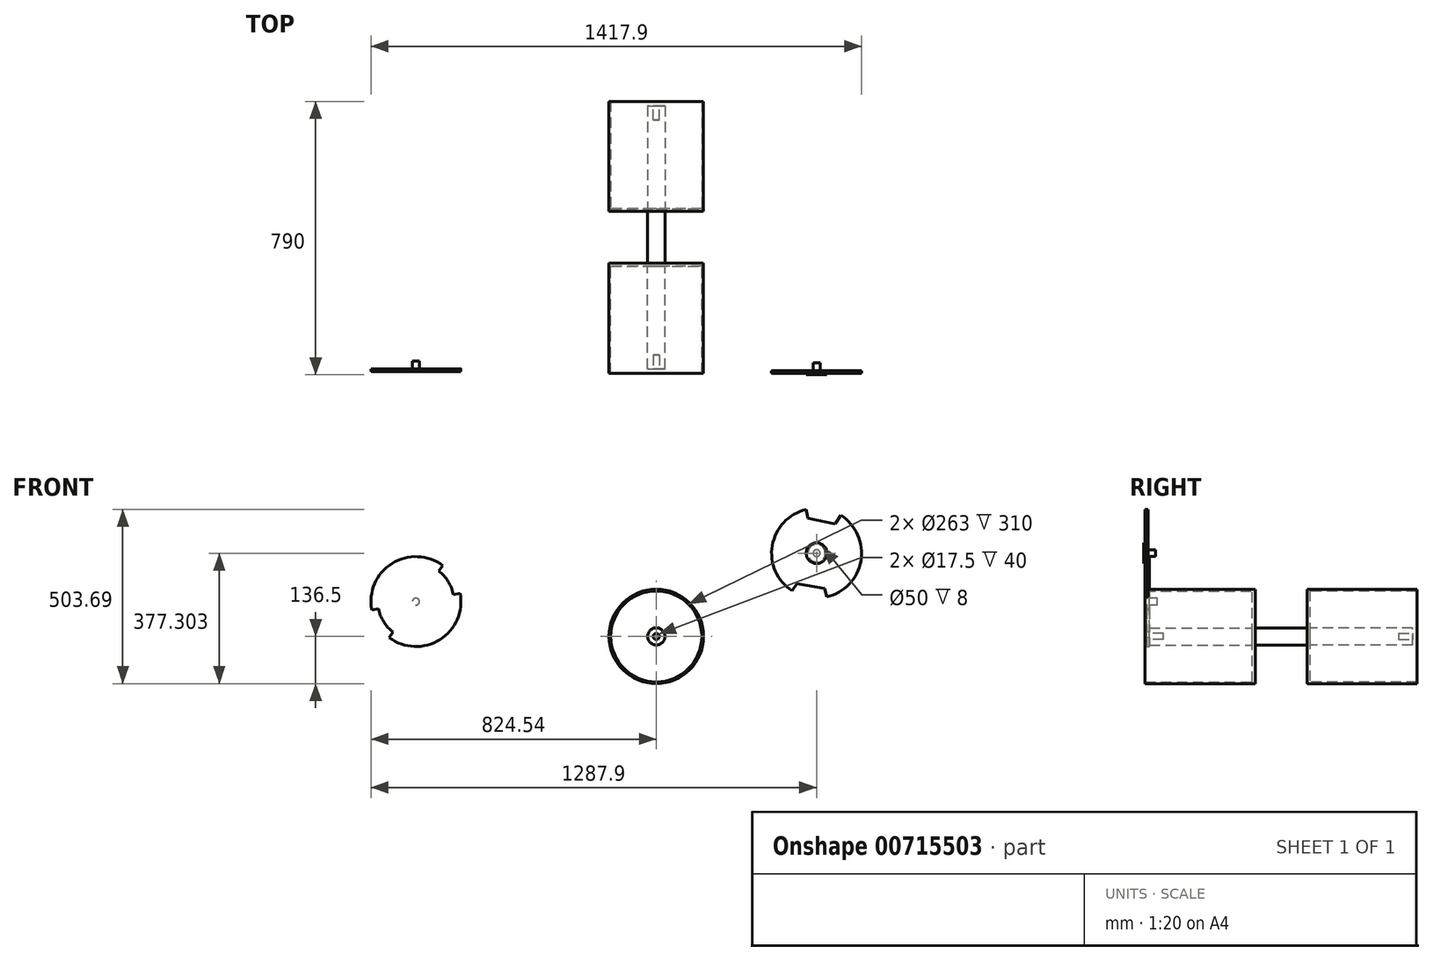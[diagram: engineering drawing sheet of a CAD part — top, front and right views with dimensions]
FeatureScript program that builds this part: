
annotation { "Feature Type Name" : "Feature", "Feature Type Description" : "" }
export const myFeature = defineFeature(function(context is Context, id is Id, definition is map)
    precondition{}
    {
        {
            var Q0;
            Q0=qCreatedBy(makeId("Front.planeOp"),FACE);
            var sketch = newSketch(context, id + "F0", { "sketchPlane" : qUnion([Q0])});
            skCircle(sketch, "E0", {"center": v(0, 0) * mm, "radius": 25 * mm});
            skSolve(sketch);
        }
        {
            var Q0;
            Q0 = qSketchRegion(id + "F0", true);
            extrude(context, id + "F1", {"entities" : qUnion([Q0]), "depth" : 75 * mm, "offsetDistance" : 25 * mm});
        }
        {
            var Q0;
            Q0=makeQuery(id+"F1.opExtrude","CAP_FACE",FACE,{"disambiguationData":[OSD([sQuery(id+"F0.wireOp",EDGE,"E0")])],"isStart":false});
            var sketch = newSketch(context, id + "F2", { "sketchPlane" : qUnion([Q0])});
            skCircle(sketch, "E1", {"center": v(0, 0) * mm, "radius": 136.5 * mm});
            skSolve(sketch);
        }
        {
            var Q0;
            Q0 = qSketchRegion(id + "F2", true);
            extrude(context, id + "F3", {"entities" : qUnion([Q0]), "operationType" : NewBodyOperationType.ADD, "depth" : 8 * mm, "offsetDistance" : 25 * mm});
        }
        {
            var Q0;
            Q0=makeQuery(id+"F3.opExtrude","CAP_FACE",FACE,{"disambiguationData":[OSD([sQuery(id+"F2.wireOp",EDGE,"E1")])],"isStart":false});
            var sketch = newSketch(context, id + "F4", { "sketchPlane" : qUnion([Q0])});
            skCircle(sketch, "E2", {"center": v(0, 0) * mm, "radius": 136.5 * mm});
            skCircle(sketch, "E3", {"center": v(0, 0) * mm, "radius": 131.5 * mm});
            skSolve(sketch);
        }
        {
            var Q0;
            Q0 = qSketchRegion(id + "F4", true);
            extrude(context, id + "F5", {"entities" : qUnion([Q0]), "operationType" : NewBodyOperationType.ADD, "depth" : 310 * mm, "offsetDistance" : 25 * mm});
        }
        {
            var Q0;
            Q0 = qSketchRegion(id + "F0", true);
            extrude(context, id + "F6", {"entities" : qUnion([Q0]), "operationType" : NewBodyOperationType.ADD, "depth" : 380 * mm, "offsetDistance" : 25 * mm});
        }
        {
            var Q0;
            Q0 = qSketchRegion(id + "F0", true);
            extrude(context, id + "F7", {"entities" : qUnion([Q0]), "operationType" : NewBodyOperationType.ADD, "oppositeDirection" : true, "depth" : 75 * mm, "offsetDistance" : 25 * mm});
        }
        {
            var Q0;
            Q0=makeQuery(id+"F7.opExtrude","CAP_FACE",FACE,{"disambiguationData":[OSD([sQuery(id+"F0.wireOp",EDGE,"E0")])],"isStart":false});
            var sketch = newSketch(context, id + "F8", { "sketchPlane" : qUnion([Q0])});
            skCircle(sketch, "E4", {"center": v(0, 0) * mm, "radius": 136.5 * mm});
            skSolve(sketch);
        }
        {
            var Q0;
            Q0 = qSketchRegion(id + "F8", true);
            extrude(context, id + "F9", {"entities" : qUnion([Q0]), "operationType" : NewBodyOperationType.ADD, "depth" : 8 * mm, "offsetDistance" : 25 * mm});
        }
        {
            var Q0;
            Q0=makeQuery(id+"F9.opExtrude","CAP_FACE",FACE,{"disambiguationData":[OSD([sQuery(id+"F8.wireOp",EDGE,"E4")])],"isStart":false});
            var sketch = newSketch(context, id + "F10", { "sketchPlane" : qUnion([Q0])});
            skCircle(sketch, "E5", {"center": v(0, 0) * mm, "radius": 136.5 * mm});
            skCircle(sketch, "E6", {"center": v(0, 0) * mm, "radius": 131.5 * mm});
            skSolve(sketch);
        }
        {
            var Q0;
            Q0 = qSketchRegion(id + "F10", true);
            extrude(context, id + "F11", {"entities" : qUnion([Q0]), "operationType" : NewBodyOperationType.ADD, "depth" : 310 * mm, "offsetDistance" : 25 * mm});
        }
        {
            var Q0;
            Q0 = qSketchRegion(id + "F0", true);
            extrude(context, id + "F12", {"entities" : qUnion([Q0]), "operationType" : NewBodyOperationType.ADD, "oppositeDirection" : true, "depth" : 380 * mm, "offsetDistance" : 25 * mm});
        }
        {
            var Q0;
            Q0=makeQuery(id+"F12.opExtrude","CAP_FACE",FACE,{"disambiguationData":[OSD([sQuery(id+"F0.wireOp",EDGE,"E0")])],"isStart":false});
            var sketch = newSketch(context, id + "F13", { "sketchPlane" : qUnion([Q0])});
            skCircle(sketch, "E7", {"center": v(0, 0) * mm, "radius": 8.75 * mm});
            skSolve(sketch);
        }
        {
            var Q0;
            Q0 = qSketchRegion(id + "F13", true);
            extrude(context, id + "F14", {"entities" : qUnion([Q0]), "operationType" : NewBodyOperationType.REMOVE, "oppositeDirection" : true, "depth" : 40 * mm, "offsetDistance" : 25 * mm});
        }
        {
            var Q0;
            Q0=makeQuery(id+"F6.opExtrude","CAP_FACE",FACE,{"disambiguationData":[OSD([sQuery(id+"F0.wireOp",EDGE,"E0")])],"isStart":false});
            var sketch = newSketch(context, id + "F15", { "sketchPlane" : qUnion([Q0])});
            skCircle(sketch, "E8", {"center": v(0, 0) * mm, "radius": 8.75 * mm});
            skSolve(sketch);
        }
        {
            var Q0;
            Q0 = qSketchRegion(id + "F15", true);
            extrude(context, id + "F16", {"entities" : qUnion([Q0]), "operationType" : NewBodyOperationType.REMOVE, "oppositeDirection" : true, "depth" : 40 * mm, "offsetDistance" : 25 * mm});
        }
        {
            var Q0;
            Q0=makeQuery(id+"F6.opExtrude","CAP_FACE",FACE,{"disambiguationData":[OSD([sQuery(id+"F0.wireOp",EDGE,"E0")])],"isStart":false});
            var sketch = newSketch(context, id + "F17", { "sketchPlane" : qUnion([Q0])});
            skCircle(sketch, "E9", {"center": v(-694.54, 100.8) * mm, "radius": 130 * mm});
            skCircle(sketch, "E10", {"center": v(-694.54, 100.8) * mm, "radius": 10 * mm});
            skSolve(sketch);
        }
        {
            var Q0;
            Q0 = qSketchRegion(id + "F17", true);
            extrude(context, id + "F18", {"entities" : qUnion([Q0]), "depth" : 8 * mm, "offsetDistance" : 25 * mm});
        }
        {
            var Q0;
            Q0=makeQuery(id+"F18.opExtrude","CAP_FACE",FACE,{"disambiguationData":[OSD([sQuery(id+"F17.wireOp",EDGE,"E9"),sQuery(id+"F17.wireOp",EDGE,"E10")])],"isStart":false});
            var sketch = newSketch(context, id + "F19", { "sketchPlane" : qUnion([Q0])});
            skArc(sketch, "E11", {"start": v(-629.03, 189.16) * mm, "mid": v(-601.38, 159.29) * mm, "end": v(-586.5, 121.4) * mm});
            skArc(sketch, "E12", {"start": v(-802.6, 80.19) * mm, "mid": v(-787.7, 42.3) * mm, "end": v(-760.06, 12.43) * mm});
            skArc(sketch, "E13", {"start": v(-566.85, 125.15) * mm, "mid": v(-584.45, 169.92) * mm, "end": v(-617.12, 205.22) * mm});
            skArc(sketch, "E14", {"start": v(-771.97, -3.63) * mm, "mid": v(-804.64, 31.67) * mm, "end": v(-822.24, 76.44) * mm});
            skLineSegment(sketch, "E15", {"start": v(-822.24, 76.44) * mm, "end": v(-802.6, 80.19) * mm});
            skLineSegment(sketch, "E16", {"start": v(-586.5, 121.4) * mm, "end": v(-566.85, 125.15) * mm});
            skLineSegment(sketch, "E17", {"start": v(-771.97, -3.63) * mm, "end": v(-760.06, 12.43) * mm});
            skLineSegment(sketch, "E18", {"start": v(-629.03, 189.16) * mm, "end": v(-617.12, 205.22) * mm});
            skSolve(sketch);
        }
        {
            var Q0;
            Q0 = qSketchRegion(id + "F19", true);
            extrude(context, id + "F20", {"entities" : qUnion([Q0]), "operationType" : NewBodyOperationType.REMOVE, "oppositeDirection" : true, "depth" : 25 * mm, "offsetDistance" : 25 * mm});
        }
        {
            var Q0;
            Q0=makeQuery(id+"F18.opExtrude","CAP_FACE",FACE,{"disambiguationData":[OSD([sQuery(id+"F17.wireOp",EDGE,"E9"),sQuery(id+"F17.wireOp",EDGE,"E10")])],"isStart":false});
            var sketch = newSketch(context, id + "F21", { "sketchPlane" : qUnion([Q0])});
            skCircle(sketch, "E19", {"center": v(-694.54, 100.8) * mm, "radius": 10 * mm});
            skSolve(sketch);
        }
        {
            var Q0;
            Q0 = qSketchRegion(id + "F21", true);
            extrude(context, id + "F22", {"entities" : qUnion([Q0]), "operationType" : NewBodyOperationType.ADD, "oppositeDirection" : true, "depth" : 30 * mm, "offsetDistance" : 25 * mm});
        }
        {
            var Q0;
            Q0=makeQuery(id+"F5.opExtrude","CAP_FACE",FACE,{"disambiguationData":[OSD([sQuery(id+"F4.wireOp",EDGE,"E2"),sQuery(id+"F4.wireOp",EDGE,"E3")])],"isStart":false});
            var sketch = newSketch(context, id + "F23", { "sketchPlane" : qUnion([Q0])});
            skCircle(sketch, "E20", {"center": v(463.36, 240.8) * mm, "radius": 130 * mm});
            skCircle(sketch, "E21", {"center": v(463.36, 240.8) * mm, "radius": 25 * mm});
            skSolve(sketch);
        }
        {
            var Q0;
            Q0 = qSketchRegion(id + "F23", true);
            extrude(context, id + "F24", {"entities" : qUnion([Q0]), "oppositeDirection" : true, "depth" : 8 * mm, "offsetDistance" : 25 * mm});
        }
        {
            var Q0;
            Q0=makeQuery(id+"F24.opExtrude","CAP_FACE",FACE,{"disambiguationData":[OSD([sQuery(id+"F23.wireOp",EDGE,"E20"),sQuery(id+"F23.wireOp",EDGE,"E21")])],"isStart":true});
            var sketch = newSketch(context, id + "F25", { "sketchPlane" : qUnion([Q0])});
            skCircle(sketch, "E22", {"center": v(463.36, 240.8) * mm, "radius": 30 * mm});
            skSolve(sketch);
        }
        {
            var Q0;
            Q0 = qSketchRegion(id + "F25", true);
            extrude(context, id + "F26", {"entities" : qUnion([Q0]), "operationType" : NewBodyOperationType.ADD, "depth" : 4 * mm, "offsetDistance" : 25 * mm});
        }
        {
            var Q0;
            Q0=makeQuery(id+"F26.opExtrude","CAP_FACE",FACE,{"disambiguationData":[OSD([sQuery(id+"F25.wireOp",EDGE,"E22")])],"isStart":true});
            var sketch = newSketch(context, id + "F27", { "sketchPlane" : qUnion([Q0])});
            skCircle(sketch, "E23", {"center": v(-463.36, 240.8) * mm, "radius": 10 * mm});
            skSolve(sketch);
        }
        {
            var Q0;
            Q0 = qSketchRegion(id + "F27", true);
            extrude(context, id + "F28", {"entities" : qUnion([Q0]), "operationType" : NewBodyOperationType.ADD, "depth" : 30 * mm, "offsetDistance" : 25 * mm});
        }
        {
            var Q0;
            Q0=makeQuery(id+"F24.opExtrude","CAP_FACE",FACE,{"disambiguationData":[OSD([sQuery(id+"F23.wireOp",EDGE,"E20"),sQuery(id+"F23.wireOp",EDGE,"E21")])],"isStart":true});
            var sketch = newSketch(context, id + "F29", { "sketchPlane" : qUnion([Q0])});
            skLineSegment(sketch, "E24", {"start": v(392.6, 131.76) * mm, "end": v(406.09, 152.8) * mm});
            skLineSegment(sketch, "E25", {"start": v(432.94, 367.2) * mm, "end": v(438.83, 342.2) * mm});
            skLineSegment(sketch, "E26", {"start": v(406.09, 152.8) * mm, "end": v(486.85, 138.46) * mm});
            skLineSegment(sketch, "E27", {"start": v(438.83, 342.2) * mm, "end": v(516.9, 325.62) * mm});
            skArc(sketch, "E28", {"start": v(392.6, 131.76) * mm, "mid": v(440.8, 112.78) * mm, "end": v(492.6, 114.13) * mm});
            skArc(sketch, "E29.trimOffspring", {"start": v(532.94, 350.62) * mm, "mid": v(484.62, 369.05) * mm, "end": v(432.94, 367.2) * mm});
            skLineSegment(sketch, "E30.trimOffspring", {"start": v(516.9, 325.62) * mm, "end": v(532.94, 350.62) * mm});
            skLineSegment(sketch, "E31.trimOffspring", {"start": v(486.85, 138.46) * mm, "end": v(492.6, 114.13) * mm});
            skSolve(sketch);
        }
        {
            var Q0;
            Q0 = qSketchRegion(id + "F29", true);
            extrude(context, id + "F30", {"entities" : qUnion([Q0]), "operationType" : NewBodyOperationType.REMOVE, "oppositeDirection" : true, "depth" : 25 * mm, "offsetDistance" : 25 * mm});
        }
    });
